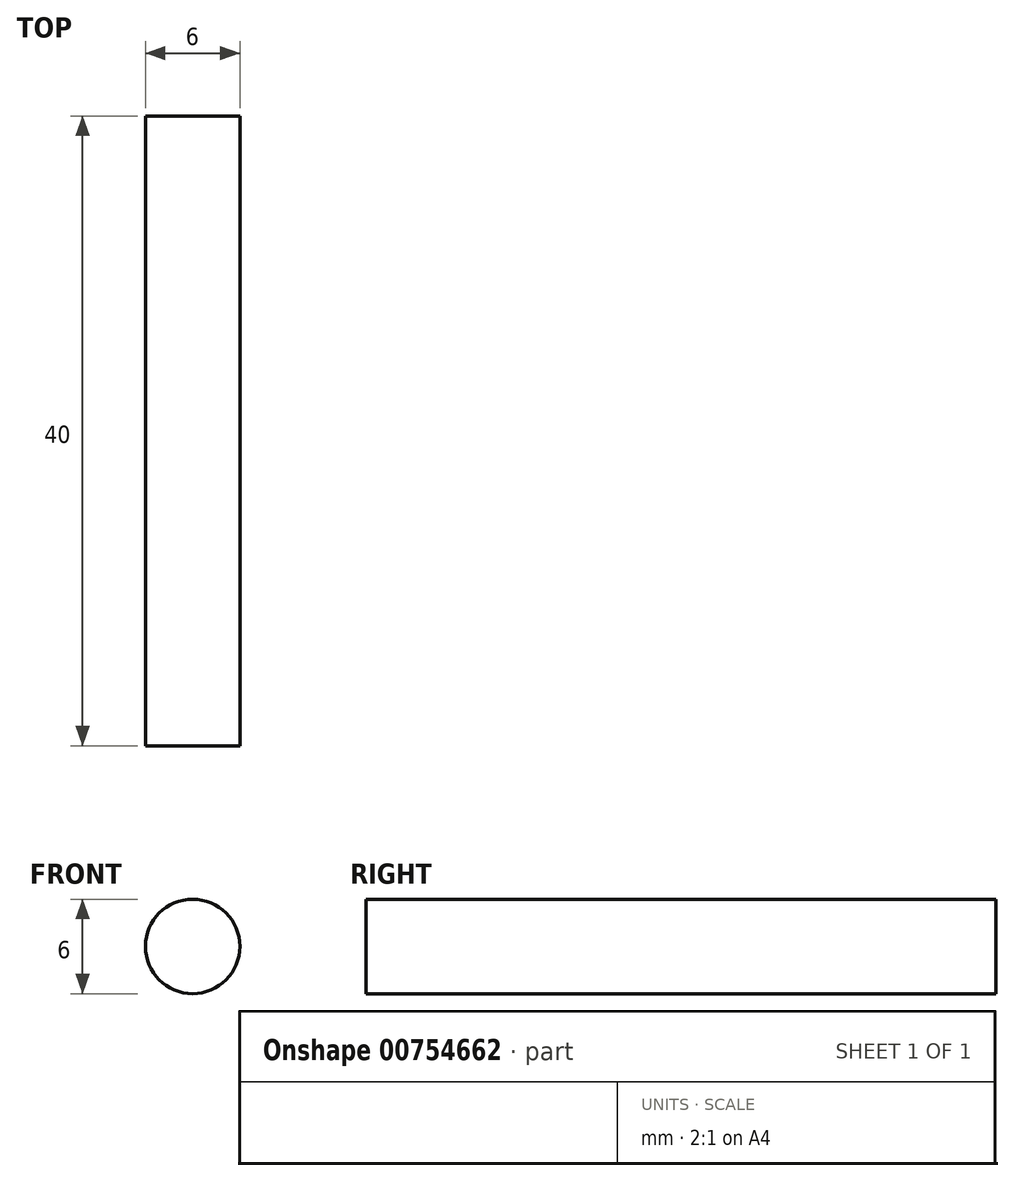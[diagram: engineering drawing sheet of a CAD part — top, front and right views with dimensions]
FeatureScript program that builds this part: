
annotation { "Feature Type Name" : "Feature", "Feature Type Description" : "" }
export const myFeature = defineFeature(function(context is Context, id is Id, definition is map)
    precondition{}
    {
        {
            var Q0;
            Q0=qCreatedBy(makeId("Front.planeOp"),FACE);
            var sketch = newSketch(context, id + "F0", { "sketchPlane" : qUnion([Q0])});
            skCircle(sketch, "E0", {"center": v(0, 0) * mm, "radius": 3 * mm});
            skSolve(sketch);
        }
        {
            var Q0;
            Q0 = qSketchRegion(id + "F0", true);
            extrude(context, id + "F1", {"entities" : qUnion([Q0]), "depth" : 40 * mm, "offsetDistance" : 25 * mm});
        }
    });
